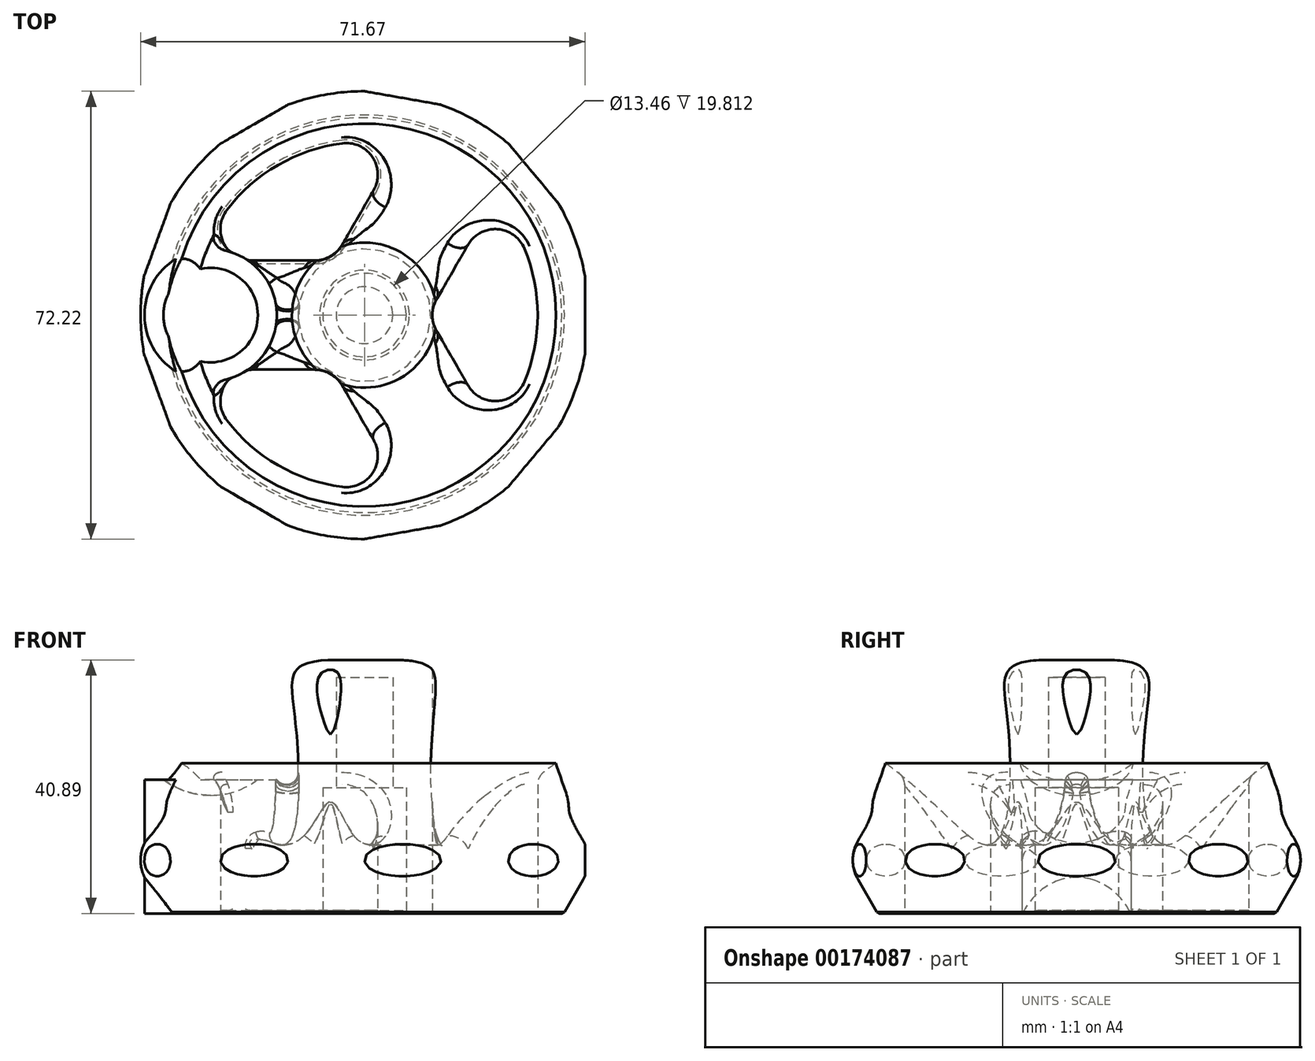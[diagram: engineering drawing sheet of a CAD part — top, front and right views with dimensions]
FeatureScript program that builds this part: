
annotation { "Feature Type Name" : "Feature", "Feature Type Description" : "" }
export const myFeature = defineFeature(function(context is Context, id is Id, definition is map)
    precondition{}
    {
        {
            var Q0;
            Q0=qCreatedBy(makeId("Front.planeOp"),FACE);
            var sketch = newSketch(context, id + "F0", { "sketchPlane" : qUnion([Q0])});
            skLineSegment(sketch, "E0", {"start": v(6.73, 0) * mm, "end": v(32.13, 0) * mm});
            skLineSegment(sketch, "E1", {"start": v(0, 40.64) * mm, "end": v(0, 38.1) * mm});
            skLineSegment(sketch, "E2", {"start": v(0, 38.1) * mm, "end": v(4.57, 38.1) * mm});
            skLineSegment(sketch, "E3", {"start": v(6.73, 20.32) * mm, "end": v(6.73, 0) * mm});
            skFitSpline(sketch, "E4", {"points": [v(35.65, 24.88) * mm, v(14.9, 11.07) * mm, v(10.97, 29.16) * mm, v(10.85, 39.41) * mm, v(0, 40.64) * mm], "startDerivative": vector(-45.35, 35.18) * mm, "endDerivative": vector(-73, -6.21) * mm});
            skPoint(sketch, "E5.orphan", {"position": v(0, 77.97) * mm});
            skLineSegment(sketch, "E6", {"start": v(0, -42.76) * mm, "end": v(0, 58.59) * mm, "construction": true});
            skLineSegment(sketch, "E7", {"start": v(4.57, 38.1) * mm, "end": v(4.57, 20.32) * mm});
            skLineSegment(sketch, "E8", {"start": v(4.57, 20.32) * mm, "end": v(6.73, 20.32) * mm});
            skPoint(sketch, "E9.orphan", {"position": v(11.05, 17.05) * mm});
            skLineSegment(sketch, "E10", {"start": v(32.13, 0) * mm, "end": v(35.26, 5.42) * mm});
            skPoint(sketch, "E11.visualSharp", {"position": v(28.42, 22.4) * mm});
            skPoint(sketch, "E12.visualSharp", {"position": v(35.56, 5.94) * mm});
            skLineSegment(sketch, "E13", {"start": v(37.21, 8.8) * mm, "end": v(30.06, 35.48) * mm, "construction": true});
            skFitSpline(sketch, "E14", {"points": [v(37.21, 8.8) * mm, v(32.84, 18.2) * mm, v(30.88, 24.23) * mm], "startDerivative": vector(-26.8, 39.37) * mm, "endDerivative": vector(-3.75, 13.08) * mm});
            skArc(sketch, "E15.filletArc", {"start": v(33.08, 16.25) * mm, "mid": v(29.56, 20.04) * mm, "end": v(24.55, 18.79) * mm});
            skArc(sketch, "E16.filletArc", {"start": v(35.26, 5.42) * mm, "mid": v(36.11, 8.69) * mm, "end": v(35.16, 11.93) * mm});
            skSolve(sketch);
        }
        {
            var Q0;
            Q0 = qSketchRegion(id + "F0", true);
            var Q1;
            Q1=sQuery(id+"F0.wireOp",EDGE,"E6");
            revolve(context, id + "F1", {"entities" : qUnion([Q0]), "axis" : qUnion([Q1]), "revolveType" : RevolveType.SYMMETRIC, "angle" : 120 * degree});
        }
        {
            var Q0;
            Q0=qCreatedBy(makeId("Top.planeOp"),FACE);
            var sketch = newSketch(context, id + "F2", { "sketchPlane" : qUnion([Q0])});
            skArc(sketch, "E17", {"start": v(25.8, -10.75) * mm, "mid": v(27.94, 0) * mm, "end": v(25.8, 10.75) * mm});
            skLineSegment(sketch, "E18", {"start": v(11.63, 2.54) * mm, "end": v(16.7, 11.33) * mm});
            skLineSegment(sketch, "E19", {"start": v(11.63, -2.54) * mm, "end": v(16.7, -11.33) * mm});
            skPoint(sketch, "E20.visualSharp", {"position": v(20.88, 18.57) * mm});
            skArc(sketch, "E20.filletArc", {"start": v(25.8, 10.75) * mm, "mid": v(21.43, 13.86) * mm, "end": v(16.7, 11.33) * mm});
            skPoint(sketch, "E21.visualSharp", {"position": v(20.88, -18.57) * mm});
            skArc(sketch, "E21.filletArc", {"start": v(16.7, -11.33) * mm, "mid": v(21.43, -13.86) * mm, "end": v(25.8, -10.75) * mm});
            skPoint(sketch, "E22.visualSharp", {"position": v(10.16, 0) * mm});
            skArc(sketch, "E22.filletArc", {"start": v(11.63, 2.54) * mm, "mid": v(10.95, 0) * mm, "end": v(11.63, -2.54) * mm});
            skSolve(sketch);
        }
        {
            var Q0;
            Q0 = qSketchRegion(id + "F2", true);
            extrude(context, id + "F3", {"entities" : qUnion([Q0]), "operationType" : NewBodyOperationType.REMOVE, "endBound" : BoundingType.THROUGH_ALL, "depth" : 25.4 * mm});
        }
        {
            var Q0;
            Q0=makeQuery(id+"F3.boolean.opBoolean","INTERSECT",EDGE,{"derivedFrom":[makeQuery(id+"F1.opRevolve","SWEPT_FACE",FACE,{"disambiguationData":[OSD([sQuery(id+"F0.wireOp",EDGE,"E4")])]}),makeQuery(id+"F3.opExtrude","SWEPT_FACE",FACE,{"disambiguationData":[OSD([sQuery(id+"F2.wireOp",EDGE,"E17")])]})]});
            fillet(context, id + "F4", {"entities" : qUnion([Q0]), "radius" : 2.54 * mm, "tangentPropagation" : true, "allowEdgeOverflow" : false});
        }
        {
            var Q0;
            Q0=qCreatedBy(makeId("Top.planeOp"),FACE);
            var sketch = newSketch(context, id + "F5", { "sketchPlane" : qUnion([Q0])});
            skLineSegment(sketch, "E23", {"start": v(35.56, -10.16) * mm, "end": v(35.56, 10.16) * mm});
            skLineSegment(sketch, "E24", {"start": v(35.56, 10.16) * mm, "end": v(39.7, 10.16) * mm});
            skLineSegment(sketch, "E25", {"start": v(39.7, 10.16) * mm, "end": v(39.7, -10.16) * mm});
            skLineSegment(sketch, "E26", {"start": v(39.7, -10.16) * mm, "end": v(35.56, -10.16) * mm});
            skSolve(sketch);
        }
        {
            var Q0;
            Q0 = qSketchRegion(id + "F5", true);
            extrude(context, id + "F6", {"entities" : qUnion([Q0]), "depth" : 25.4 * mm});
        }
        {
            var Q0;
            Q0=makeQuery(id+"F6.opExtrude","SWEPT_BODY",BODY,{"disambiguationData":[OSD([sQuery(id+"F5.wireOp",EDGE,"E23"),sQuery(id+"F5.wireOp",EDGE,"E24"),sQuery(id+"F5.wireOp",EDGE,"E25"),sQuery(id+"F5.wireOp",EDGE,"E26")])]});
            var Q1;
            Q1=sQuery(id+"F0.wireOp",EDGE,"E6");
            circularPattern(context, id + "F7", {"operationType" : NewBodyOperationType.REMOVE, "entities" : qUnion([Q0]), "axis" : qUnion([Q1]), "angle" : 360 * degree, "instanceCount" : 9, "equalSpace" : true});
        }
        {
            var Q0;
            Q0=makeQuery(id+"F1.opRevolve","SWEPT_BODY",BODY,{"disambiguationData":[OSD([sQuery(id+"F0.wireOp",EDGE,"E0"),sQuery(id+"F0.wireOp",EDGE,"dpCK8SRb-WdQn-L2Cs-7aav-e22ffPn0EV3C"),sQuery(id+"F0.wireOp",EDGE,"99iCUp3l-W3Re-Ts3m-6MKF-OaPGGpgDnCRw"),sQuery(id+"F0.wireOp",EDGE,"E1"),sQuery(id+"F0.wireOp",EDGE,"E2"),sQuery(id+"F0.wireOp",EDGE,"E3"),sQuery(id+"F0.wireOp",EDGE,"E4")])]});
            var Q1;
            Q1=sQuery(id+"F0.wireOp",EDGE,"E6");
            circularPattern(context, id + "F8", {"operationType" : NewBodyOperationType.ADD, "entities" : qUnion([Q0]), "axis" : qUnion([Q1]), "angle" : 360 * degree, "instanceCount" : 3, "equalSpace" : true});
        }
        {
            var Q0;
            Q0=makeQuery(id+"F8.opPattern","COPY",FACE,{"derivedFrom":makeQuery(id+"F3.boolean.opBoolean","COPY",FACE,{"derivedFrom":makeQuery(id+"F3.opExtrude","SWEPT_FACE",FACE,{"disambiguationData":[OSD([sQuery(id+"F2.wireOp",EDGE,"E18")])]})}),"instanceName":"1"});
            var Q1;
            {var subQ0=makeQuery(id+"F1.opRevolve","SWEPT_EDGE",EDGE,{"disambiguationData":[OSD([sQuery(id+"F0.wireOp",EDGE,"E0"),sQuery(id+"F0.wireOp",EDGE,"E3")])]});Q1=makeQuery(id+"F8.boolean.opBoolean","MERGE",EDGE,{"derivedFrom":[subQ0,makeQuery(id+"F8.opPattern","COPY",EDGE,{"derivedFrom":subQ0,"instanceName":"1"}),makeQuery(id+"F8.opPattern","COPY",EDGE,{"derivedFrom":subQ0,"instanceName":"2"})]});}
            var Q2;
            Q2=makeQuery(id+"F3.boolean.opBoolean","COPY",EDGE,{"derivedFrom":makeQuery(id+"F3.opExtrude","CAP_EDGE",EDGE,{"disambiguationData":[OSD([sQuery(id+"F2.wireOp",EDGE,"E18")])],"isStart":true})});
            var Q3;
            Q3=makeQuery(id+"F8.opPattern","COPY",EDGE,{"derivedFrom":makeQuery(id+"F3.boolean.opBoolean","COPY",EDGE,{"derivedFrom":makeQuery(id+"F3.opExtrude","CAP_EDGE",EDGE,{"disambiguationData":[OSD([sQuery(id+"F2.wireOp",EDGE,"E19")])],"isStart":true})}),"instanceName":"2"});
            var Q4;
            {var subQ0=makeQuery(id+"F1.opRevolve","SWEPT_EDGE",EDGE,{"disambiguationData":[OSD([sQuery(id+"F0.wireOp",EDGE,"E0"),sQuery(id+"F0.wireOp",EDGE,"vpSZ5KzX-oGi7-IppH-yeRc-xyXKcn8NRoAp")])]});Q4=makeQuery(id+"F8.boolean.opBoolean","MERGE",EDGE,{"derivedFrom":[subQ0,makeQuery(id+"F8.opPattern","COPY",EDGE,{"derivedFrom":subQ0,"instanceName":"1"}),makeQuery(id+"F8.opPattern","COPY",EDGE,{"derivedFrom":subQ0,"instanceName":"2"})]});}
            chamfer(context, id + "F9", {"entities" : qUnion([Q0, Q1, Q2, Q3, Q4]), "width" : 0.5 * mm, "tangentPropagation" : true});
        }
        {
            var Q0;
            Q0=qCreatedBy(makeId("Top.planeOp"),FACE);
            var sketch = newSketch(context, id + "F10", { "sketchPlane" : qUnion([Q0])});
            skCircle(sketch, "E27", {"center": v(-24.82, 0) * mm, "radius": 10.67 * mm});
            skSolve(sketch);
        }
        {
            var Q0;
            Q0 = qSketchRegion(id + "F10", true);
            extrude(context, id + "F11", {"entities" : qUnion([Q0]), "operationType" : NewBodyOperationType.ADD, "depth" : 21.59 * mm});
        }
        {
            var Q0;
            Q0=qCreatedBy(makeId("Front.planeOp"),FACE);
            var sketch = newSketch(context, id + "F12", { "sketchPlane" : qUnion([Q0])});
            skLineSegment(sketch, "E28", {"start": v(-24.82, 21.59) * mm, "end": v(-24.82, 38.4) * mm, "construction": true});
            skLineSegment(sketch, "E29", {"start": v(-24.82, 31.75) * mm, "end": v(-24.82, 19.05) * mm});
            skArc(sketch, "E30", {"start": v(-37.52, 31.75) * mm, "mid": v(-33.8, 22.77) * mm, "end": v(-24.82, 19.05) * mm});
            skPoint(sketch, "E31.orphan", {"position": v(-32.35, 21.59) * mm});
            skLineSegment(sketch, "E32", {"start": v(-24.82, 19.05) * mm, "end": v(-24.82, 31.75) * mm});
            skLineSegment(sketch, "E33", {"start": v(-37.52, 31.75) * mm, "end": v(-24.82, 31.75) * mm});
            skSolve(sketch);
        }
        {
            var Q0;
            Q0 = qSketchRegion(id + "F12", true);
            var Q1;
            Q1=sQuery(id+"F12.wireOp",EDGE,"E28");
            revolve(context, id + "F13", {"operationType" : NewBodyOperationType.REMOVE, "entities" : qUnion([Q0]), "axis" : qUnion([Q1]), "revolveType" : RevolveType.FULL, "oppositeDirection" : true});
        }
        {
            var Q0;
            {var subQ0=makeQuery(id+"F1.opRevolve","SWEPT_FACE",FACE,{"disambiguationData":[OSD([sQuery(id+"F0.wireOp",EDGE,"E4")])]});Q0=makeQuery(id+"F11.boolean.opBoolean","INTERSECT",EDGE,{"derivedFrom":[makeQuery(id+"F8.boolean.opBoolean","MERGE",FACE,{"derivedFrom":[subQ0,makeQuery(id+"F8.opPattern","COPY",FACE,{"derivedFrom":subQ0,"instanceName":"1"}),makeQuery(id+"F8.opPattern","COPY",FACE,{"derivedFrom":subQ0,"instanceName":"2"})]}),makeQuery(id+"F11.opExtrude","SWEPT_FACE",FACE,{"disambiguationData":[OSD([sQuery(id+"F10.wireOp",EDGE,"E27")])]})]});}
            var Q1;
            {var subQ0=makeQuery(id+"F1.opRevolve","SWEPT_FACE",FACE,{"disambiguationData":[OSD([sQuery(id+"F0.wireOp",EDGE,"E15.filletArc")])]});Q1=makeQuery(id+"F11.boolean.opBoolean","INTERSECT",EDGE,{"disambiguationData":[OD(1.0)],"derivedFrom":[makeQuery(id+"F8.boolean.opBoolean","MERGE",FACE,{"derivedFrom":[subQ0,makeQuery(id+"F8.opPattern","COPY",FACE,{"derivedFrom":subQ0,"instanceName":"1"}),makeQuery(id+"F8.opPattern","COPY",FACE,{"derivedFrom":subQ0,"instanceName":"2"})]}),makeQuery(id+"F11.opExtrude","SWEPT_FACE",FACE,{"disambiguationData":[OSD([sQuery(id+"F10.wireOp",EDGE,"E27")])]})]});}
            fillet(context, id + "F14", {"entities" : qUnion([Q0, Q1]), "radius" : 1.9 * mm, "tangentPropagation" : true, "allowEdgeOverflow" : false});
        }
    });
